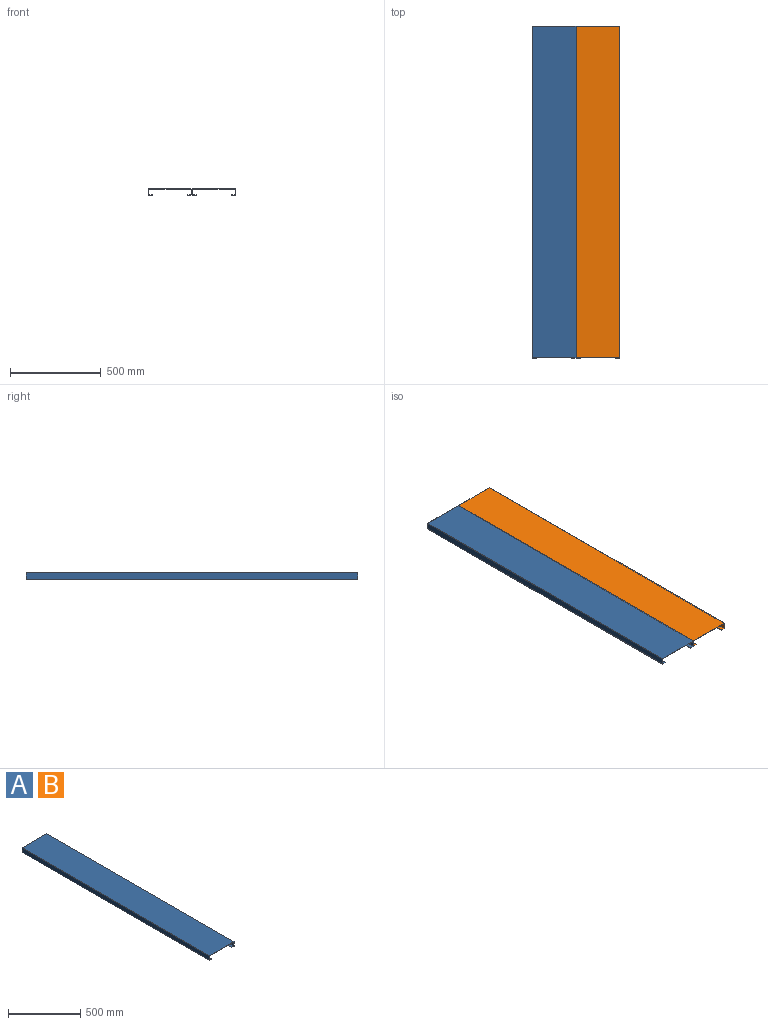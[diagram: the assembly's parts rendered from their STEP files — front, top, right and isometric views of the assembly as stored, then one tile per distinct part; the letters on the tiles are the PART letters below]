
ASSEMBLY  parts=2 mates=1
PART A: 14 faces, bbox 241.3x1828.8x38.1 mm
  f0: plane 1828.8x19.69mm, normal (0,0,1), area 35999.9mm2, adj f1,f11,f12,f13
  f1: plane 1828.8x2.54mm, normal (-1,0,0), area 4645.2mm2, adj f0,f2,f12,f13
  f2: plane 1828.8x22.23mm, normal (0,0,-1), area 40645.1mm2, adj f1,f3,f12,f13
  f3: plane 1828.8x38.1mm, normal (1,0,0), area 69677.3mm2, adj f2,f4,f12,f13
  f4: plane 1828.8x241.3mm, normal (0,0,1), area 441289.4mm2, adj f3,f5,f12,f13
  f5: plane 1828.8x38.1mm, normal (-1,0,0), area 69677.3mm2, adj f4,f6,f12,f13
  f6: plane 1828.8x22.23mm, normal (0,0,-1), area 40645.1mm2, adj f5,f7,f12,f13
  f7: plane 1828.8x2.54mm, normal (1,0,0), area 4645.2mm2, adj f6,f8,f12,f13
  f8: plane 1828.8x19.69mm, normal (0,0,1), area 35999.9mm2, adj f7,f9,f12,f13
  f9: plane 1828.8x33.02mm, normal (1,0,0), area 60387mm2, adj f8,f10,f12,f13
  f10: plane 1828.8x236.22mm, normal (0,0,-1), area 431999.1mm2, adj f9,f11,f12,f13
  f11: plane 1828.8x33.02mm, normal (-1,0,0), area 60387mm2, adj f0,f10,f12,f13
  f12: plane 241.3x38.1mm, normal (0,-1,0), area 893.5mm2, adj f0,f1,f2,f3,f4,f5,f6,f7
  f13: plane 241.3x38.1mm, normal (0,1,0), area 893.5mm2, adj f0,f1,f2,f3,f4,f5,f6,f7
PART B: same geometry as A
PLACE A t=(-134.07,-71.5,8.86)mm fixed
PLACE B t=(107.23,-71.5,8.86)mm
MATE fastened A.f3 <-> B.f5  axis (1,0,0) through (-13.42,-985.9,27.91)mm
